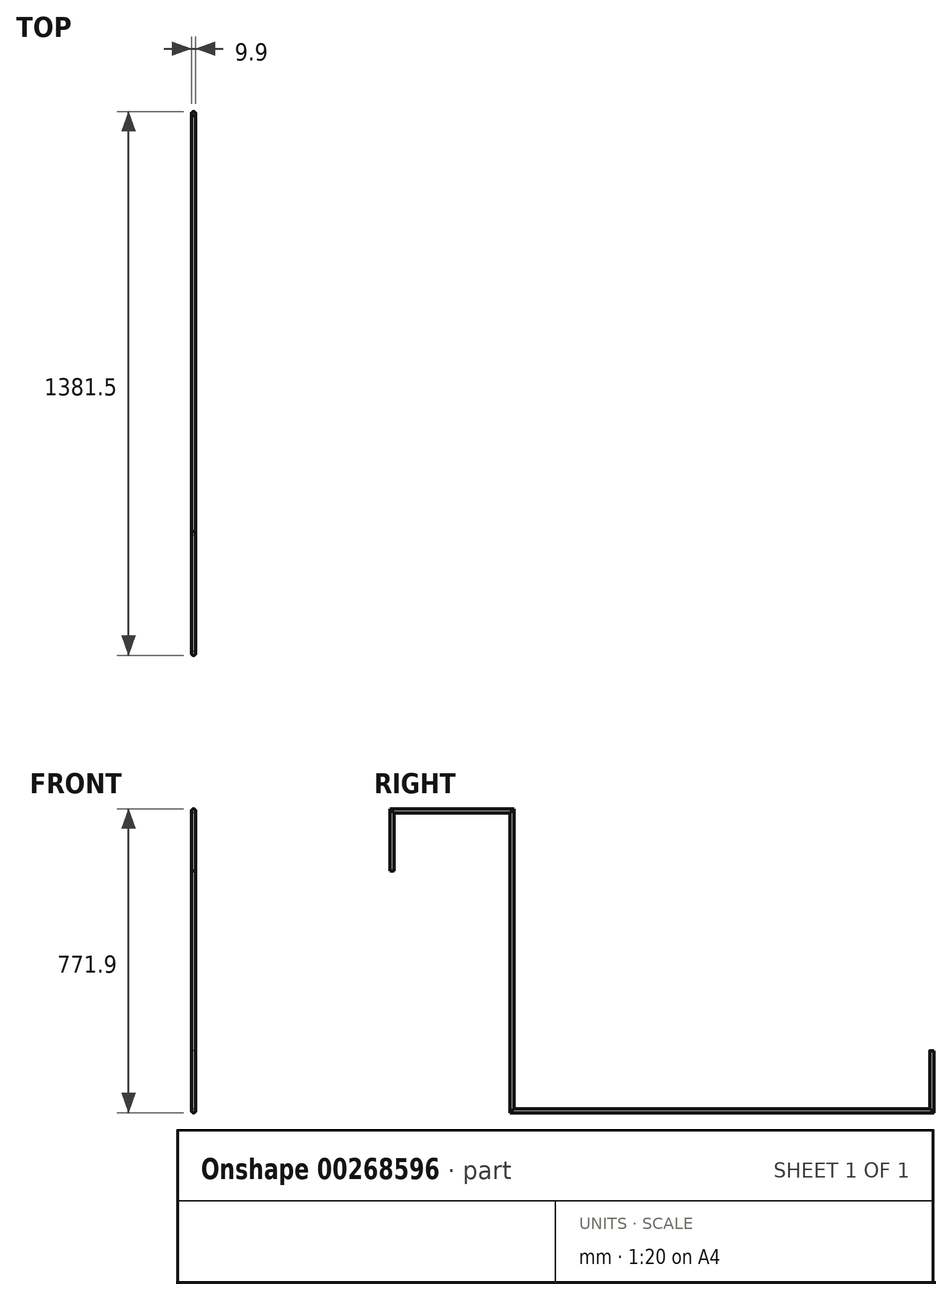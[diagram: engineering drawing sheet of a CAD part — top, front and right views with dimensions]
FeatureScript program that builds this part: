
annotation { "Feature Type Name" : "Feature", "Feature Type Description" : "" }
export const myFeature = defineFeature(function(context is Context, id is Id, definition is map)
    precondition{}
    {
        {
            var Q0;
            Q0=qCreatedBy(makeId("Top.planeOp"),FACE);
            var sketch = newSketch(context, id + "F0", { "sketchPlane" : qUnion([Q0])});
            skCircle(sketch, "E0", {"center": v(0, 0) * mm, "radius": 4.95 * mm});
            skSolve(sketch);
        }
        {
            var Q0;
            Q0=qCreatedBy(makeId("Right.planeOp"),FACE);
            var sketch = newSketch(context, id + "F1", { "sketchPlane" : qUnion([Q0])});
            skLineSegment(sketch, "E1", {"start": v(0, 0) * mm, "end": v(0, 152.4) * mm});
            skLineSegment(sketch, "E2", {"start": v(0, 152.4) * mm, "end": v(304.8, 152.4) * mm});
            skLineSegment(sketch, "E3", {"start": v(304.8, 152.4) * mm, "end": v(304.8, -609.6) * mm});
            skLineSegment(sketch, "E4", {"start": v(304.8, -609.6) * mm, "end": v(1371.6, -609.6) * mm});
            skLineSegment(sketch, "E5", {"start": v(1371.6, -609.6) * mm, "end": v(1371.6, -457.2) * mm});
            skSolve(sketch);
        }
        {
            var Q0;
            Q0 = qSketchRegion(id + "F0", true);
            var Q1;
            Q1 = qConstructionFilter(qBodyType(qCreatedBy(id + "F1" ,EDGE), BodyType.WIRE), ConstructionObject.NO);
            sweep(context, id + "F2", {"profiles" : qUnion([Q0]), "path" : qUnion([Q1])});
        }
    });
